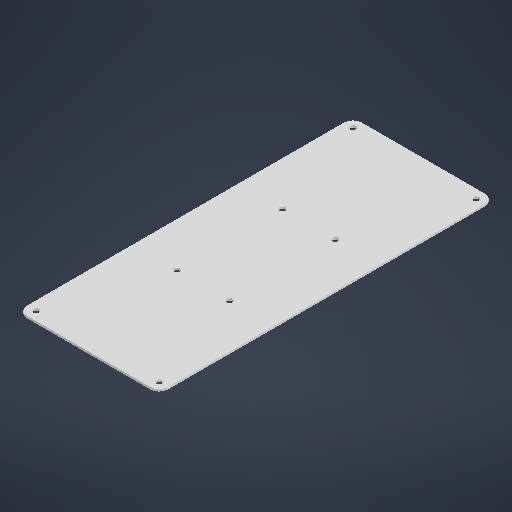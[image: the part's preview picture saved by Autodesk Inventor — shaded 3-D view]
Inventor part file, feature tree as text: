
AUTODESK INVENTOR PART (.ipt)
format: ipt  version: 2025.2 (Build 292293000, 293)  size: 190,976 bytes
history: native  units: in
note: dims shown in document units (in); Inventor stores cm internally (conversion verified against a paired STEP export)
features: extrude x1, sketch x1
ambient origin geometry x8: Origin, YZ Plane, XZ Plane, XY Plane, X Axis, Y Axis, Z Axis, Center Point
bodies: Solid1 (feature_tree)
feature tree (2):
  extrude  "Extrusion1"  Depth=0.0625in
  sketch  "Sketch1"  dims[d0=0.172in d2=0.172in d7=0.172in d8=0.172in d15=0.172in d16=0.172in d17=0.172in d18=0.172in d20=0.0625in d21=0.0in]
